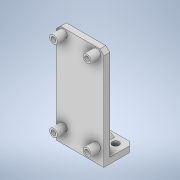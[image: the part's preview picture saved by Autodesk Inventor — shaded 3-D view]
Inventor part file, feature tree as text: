
AUTODESK INVENTOR PART (.ipt)
format: ipt  version: 2022.6 (Build 266554000, 554)  size: 210,432 bytes
history: native  units: mm
features: sketch x6, extrude x4, plane x2, hole x2, chamfer x2, projected_geometry x2, rib x1
ambient origin geometry x8: Origin, YZ Plane, XZ Plane, XY Plane, X Axis, Y Axis, Z Axis, Center Point
bodies: Solid1 (feature_tree)
feature tree (19):
  extrude  "Extrusion1"  Depth=46.0mm
  plane  "Work Plane1"
  plane  "Work Plane2"
  sketch  "Sketch2"  dims[d2=3.0mm d3=0.0mm d4=17.0mm]
  extrude  "Extrusion2"  Depth=3.0mm
  hole  "Hole1"  [1 undecoded]
  extrude  "Extrusion4"  Depth=12.0mm
  extrude  "Extrusion5"  Depth=2.5mm
  hole  "Hole3"  [1 undecoded]
  chamfer  "Chamfer1"  Distance=2.4mm
  rib  "Rib1"
  chamfer  "Chamfer3"  Distance=4.0mm
  sketch  "Sketch1"  dims[d0=24.0mm d1=46.0mm]
  sketch  "Sketch5"  dims[d6=41.0mm d7=2.5mm]
  sketch  "Sketch6"  dims[d8=3.5mm d9=12.0mm d10=23.0mm d11=3.5mm]
  sketch  "Sketch7"  dims[d12=3.5mm d13=2.5mm]
  sketch  "Sketch10"  dims[d14=41.0mm d15=4.0mm d16=2.4mm d17=4.0mm d18=2.4mm d19=4.0mm d20=2.4mm d21=2.4mm d22=4.0mm d23=5.0mm d24=0.0mm d25=2.4mm d26=6.0mm d27=4.0mm d28=2.0mm d29=90.0deg d30=8.0mm d31=20.594885mm d47=0.0mm d48=24.0mm d49=5.0mm d50=0.0mm d51=3.0mm d52=15.0mm d53=0.0mm d54=15.0mm d55=4.5mm d56=4.5mm d57=3.4mm d58=6.0mm d59=4.0mm d60=2.0mm d61=90.0deg d62=8.0mm d63=20.594885mm d65=2.0mm d66=2.0mm d67=45.0deg d74=30.0mm d75=1.0mm d76=5.0mm d77=0.0mm d78=0.0mm d79=1.0mm d80=1.0mm d84=2.0mm d85=2.0mm d86=45.0deg]
  projected_geometry  "Projected Loop4"
  projected_geometry  "Projected Loop5"
note: 2 required parameter values undecoded (feature->parameter linkage not recoverable at this tier; creation-order binding heuristic only, values carry confidence <= 0.55)
